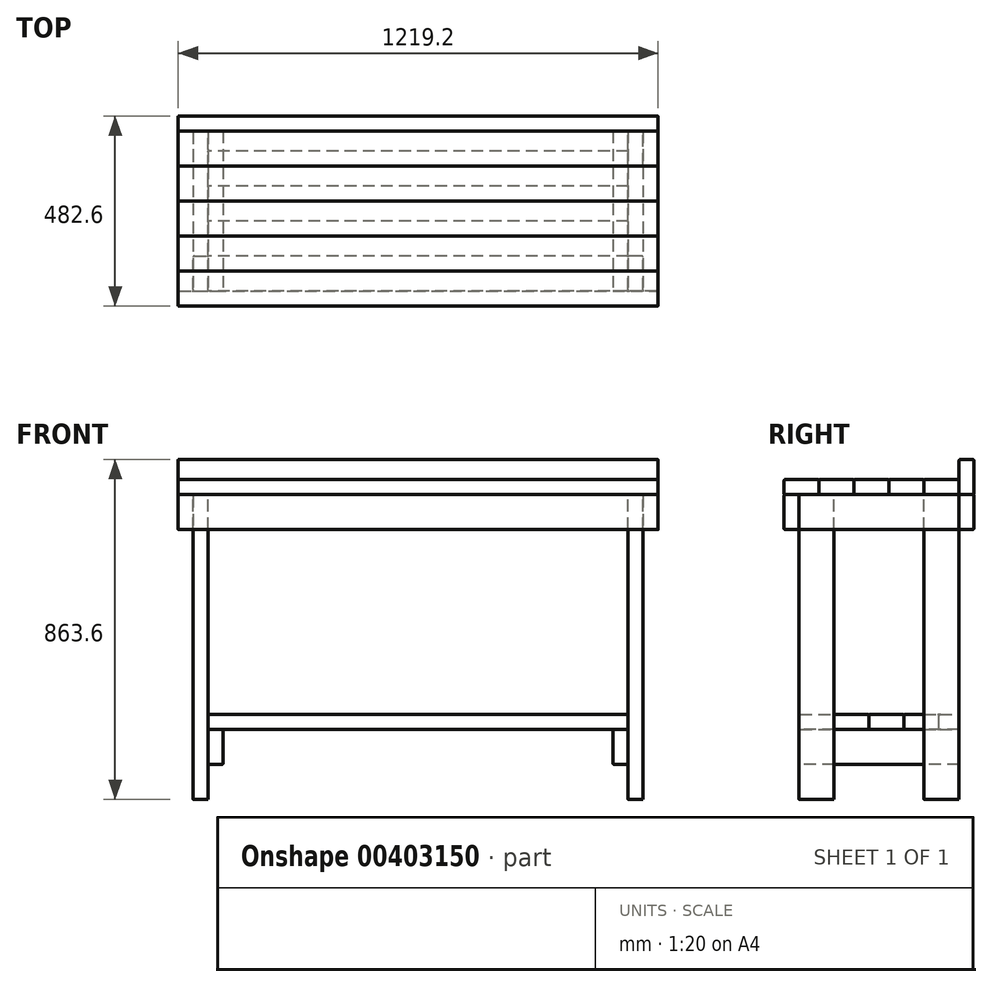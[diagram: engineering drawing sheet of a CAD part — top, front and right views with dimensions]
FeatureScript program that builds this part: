
annotation { "Feature Type Name" : "Feature", "Feature Type Description" : "" }
export const myFeature = defineFeature(function(context is Context, id is Id, definition is map)
    precondition{}
    {
        {
            var Q0;
            Q0=qCreatedBy(makeId("Right.planeOp"),FACE);
            var sketch = newSketch(context, id + "F0", { "sketchPlane" : qUnion([Q0])});
            skLineSegment(sketch, "E0.bottom", {"start": v(3.17, 0) * mm, "end": v(85.73, 0) * mm});
            skLineSegment(sketch, "E0.top", {"start": v(3.17, 38.1) * mm, "end": v(85.73, 38.1) * mm});
            skLineSegment(sketch, "E0.left", {"start": v(0, 3.18) * mm, "end": v(0, 34.93) * mm});
            skLineSegment(sketch, "E0.right", {"start": v(88.9, 3.18) * mm, "end": v(88.9, 34.93) * mm});
            skPoint(sketch, "E1.visualSharp", {"position": v(0, 38.1) * mm});
            skArc(sketch, "E1.filletArc", {"start": v(3.17, 38.1) * mm, "mid": v(0.93, 37.17) * mm, "end": v(0, 34.93) * mm});
            skPoint(sketch, "E2.visualSharp", {"position": v(0, 0) * mm});
            skArc(sketch, "E2.filletArc", {"start": v(0, 3.18) * mm, "mid": v(0.93, 0.93) * mm, "end": v(3.17, 0) * mm});
            skPoint(sketch, "E3.visualSharp", {"position": v(88.9, 0) * mm});
            skArc(sketch, "E3.filletArc", {"start": v(85.73, 0) * mm, "mid": v(87.97, 0.93) * mm, "end": v(88.9, 3.18) * mm});
            skPoint(sketch, "E4.visualSharp", {"position": v(88.9, 38.1) * mm});
            skArc(sketch, "E4.filletArc", {"start": v(88.9, 34.93) * mm, "mid": v(87.97, 37.17) * mm, "end": v(85.73, 38.1) * mm});
            skSolve(sketch);
        }
        {
            var Q0;
            Q0 = qSketchRegion(id + "F0", true);
            extrude(context, id + "F1", {"entities" : qUnion([Q0]), "depth" : 1219.2 * mm});
        }
        {
            var Q0;
            Q0=makeQuery(id+"F1.opExtrude","SWEPT_BODY",BODY,{"disambiguationData":[OSD([sQuery(id+"F0.wireOp",EDGE,"E0.bottom"),sQuery(id+"F0.wireOp",EDGE,"E0.top"),sQuery(id+"F0.wireOp",EDGE,"E0.left"),sQuery(id+"F0.wireOp",EDGE,"E0.right"),sQuery(id+"F0.wireOp",EDGE,"E1.filletArc"),sQuery(id+"F0.wireOp",EDGE,"E2.filletArc"),sQuery(id+"F0.wireOp",EDGE,"E3.filletArc"),sQuery(id+"F0.wireOp",EDGE,"E4.filletArc")])]});
            transform(context, id + "F2", {"entities" : qUnion([Q0]), "transformType" : TransformType.TRANSLATION_3D, "dx" : 0 * mm, "dy" : 88.9 * mm, "dz" : 0 * mm, "makeCopy" : true});
        }
        {
            var Q0;
            Q0=makeQuery(id+"F2.opPattern","COPY",BODY,{"derivedFrom":makeQuery(id+"F1.opExtrude","SWEPT_BODY",BODY,{"disambiguationData":[OSD([sQuery(id+"F0.wireOp",EDGE,"E0.bottom"),sQuery(id+"F0.wireOp",EDGE,"E0.top"),sQuery(id+"F0.wireOp",EDGE,"E0.left"),sQuery(id+"F0.wireOp",EDGE,"E0.right"),sQuery(id+"F0.wireOp",EDGE,"E1.filletArc"),sQuery(id+"F0.wireOp",EDGE,"E2.filletArc"),sQuery(id+"F0.wireOp",EDGE,"E3.filletArc"),sQuery(id+"F0.wireOp",EDGE,"E4.filletArc")])]}),"instanceName":"1"});
            transform(context, id + "F3", {"entities" : qUnion([Q0]), "transformType" : TransformType.TRANSLATION_3D, "dx" : 0 * mm, "dy" : 88.9 * mm, "dz" : 0 * mm, "makeCopy" : true});
        }
        {
            var Q0;
            Q0=makeQuery(id+"F3.opPattern","COPY",BODY,{"derivedFrom":makeQuery(id+"F2.opPattern","COPY",BODY,{"derivedFrom":makeQuery(id+"F1.opExtrude","SWEPT_BODY",BODY,{"disambiguationData":[OSD([sQuery(id+"F0.wireOp",EDGE,"E0.bottom"),sQuery(id+"F0.wireOp",EDGE,"E0.top"),sQuery(id+"F0.wireOp",EDGE,"E0.left"),sQuery(id+"F0.wireOp",EDGE,"E0.right"),sQuery(id+"F0.wireOp",EDGE,"E1.filletArc"),sQuery(id+"F0.wireOp",EDGE,"E2.filletArc"),sQuery(id+"F0.wireOp",EDGE,"E3.filletArc"),sQuery(id+"F0.wireOp",EDGE,"E4.filletArc")])]}),"instanceName":"1"}),"instanceName":"1"});
            transform(context, id + "F4", {"entities" : qUnion([Q0]), "transformType" : TransformType.TRANSLATION_3D, "dx" : 0 * mm, "dy" : 88.9 * mm, "dz" : 0 * mm, "makeCopy" : true});
        }
        {
            var Q0;
            Q0=makeQuery(id+"F4.opPattern","COPY",BODY,{"derivedFrom":makeQuery(id+"F3.opPattern","COPY",BODY,{"derivedFrom":makeQuery(id+"F2.opPattern","COPY",BODY,{"derivedFrom":makeQuery(id+"F1.opExtrude","SWEPT_BODY",BODY,{"disambiguationData":[OSD([sQuery(id+"F0.wireOp",EDGE,"E0.bottom"),sQuery(id+"F0.wireOp",EDGE,"E0.top"),sQuery(id+"F0.wireOp",EDGE,"E0.left"),sQuery(id+"F0.wireOp",EDGE,"E0.right"),sQuery(id+"F0.wireOp",EDGE,"E1.filletArc"),sQuery(id+"F0.wireOp",EDGE,"E2.filletArc"),sQuery(id+"F0.wireOp",EDGE,"E3.filletArc"),sQuery(id+"F0.wireOp",EDGE,"E4.filletArc")])]}),"instanceName":"1"}),"instanceName":"1"}),"instanceName":"1"});
            transform(context, id + "F5", {"entities" : qUnion([Q0]), "transformType" : TransformType.TRANSLATION_3D, "dx" : 0 * mm, "dy" : 88.9 * mm, "dz" : 0 * mm, "makeCopy" : true});
        }
        {
            var Q0;
            Q0=qCreatedBy(makeId("Right.planeOp"),FACE);
            var sketch = newSketch(context, id + "F6", { "sketchPlane" : qUnion([Q0])});
            skLineSegment(sketch, "E5.bottom", {"start": v(447.68, 0) * mm, "end": v(479.43, 0) * mm});
            skLineSegment(sketch, "E5.top", {"start": v(447.68, 88.9) * mm, "end": v(479.43, 88.9) * mm});
            skLineSegment(sketch, "E5.left", {"start": v(444.5, 3.18) * mm, "end": v(444.5, 85.73) * mm});
            skLineSegment(sketch, "E5.right", {"start": v(482.6, 3.17) * mm, "end": v(482.6, 85.73) * mm});
            skPoint(sketch, "E6.visualSharp", {"position": v(444.5, 88.9) * mm});
            skArc(sketch, "E6.filletArc", {"start": v(447.68, 88.9) * mm, "mid": v(445.43, 87.97) * mm, "end": v(444.5, 85.73) * mm});
            skPoint(sketch, "E7.visualSharp", {"position": v(482.6, 88.9) * mm});
            skArc(sketch, "E7.filletArc", {"start": v(482.6, 85.73) * mm, "mid": v(481.67, 87.97) * mm, "end": v(479.43, 88.9) * mm});
            skPoint(sketch, "E8.visualSharp", {"position": v(482.6, 0) * mm});
            skArc(sketch, "E8.filletArc", {"start": v(479.43, 0) * mm, "mid": v(481.67, 0.93) * mm, "end": v(482.6, 3.17) * mm});
            skPoint(sketch, "E9.visualSharp", {"position": v(444.5, 0) * mm});
            skArc(sketch, "E9.filletArc", {"start": v(444.5, 3.18) * mm, "mid": v(445.43, 0.93) * mm, "end": v(447.68, 0) * mm});
            skSolve(sketch);
        }
        {
            var Q0;
            Q0 = qSketchRegion(id + "F6", true);
            extrude(context, id + "F7", {"entities" : qUnion([Q0]), "depth" : 1219.2 * mm});
        }
        {
            var Q0;
            Q0=makeQuery(id+"F1.opExtrude","CAP_FACE",FACE,{"disambiguationData":[OSD([sQuery(id+"F0.wireOp",EDGE,"E0.bottom"),sQuery(id+"F0.wireOp",EDGE,"E0.top"),sQuery(id+"F0.wireOp",EDGE,"E0.left"),sQuery(id+"F0.wireOp",EDGE,"E0.right"),sQuery(id+"F0.wireOp",EDGE,"E1.filletArc"),sQuery(id+"F0.wireOp",EDGE,"E2.filletArc"),sQuery(id+"F0.wireOp",EDGE,"E3.filletArc"),sQuery(id+"F0.wireOp",EDGE,"E4.filletArc")])],"isStart":false});
            var sketch = newSketch(context, id + "F8", { "sketchPlane" : qUnion([Q0])});
            skLineSegment(sketch, "E10.bottom", {"start": v(3.18, 0) * mm, "end": v(34.93, 0) * mm});
            skLineSegment(sketch, "E10.top", {"start": v(3.18, -88.9) * mm, "end": v(34.93, -88.9) * mm});
            skLineSegment(sketch, "E10.left", {"start": v(0, -3.17) * mm, "end": v(0, -85.72) * mm});
            skLineSegment(sketch, "E10.right", {"start": v(38.1, -3.17) * mm, "end": v(38.1, -85.72) * mm});
            skPoint(sketch, "E11.visualSharp", {"position": v(0, 0) * mm});
            skArc(sketch, "E11.filletArc", {"start": v(3.18, 0) * mm, "mid": v(0.93, -0.93) * mm, "end": v(0, -3.18) * mm});
            skPoint(sketch, "E12.visualSharp", {"position": v(38.1, 0) * mm});
            skArc(sketch, "E12.filletArc", {"start": v(38.1, -3.17) * mm, "mid": v(37.17, -0.93) * mm, "end": v(34.93, 0) * mm});
            skPoint(sketch, "E13.visualSharp", {"position": v(38.1, -88.9) * mm});
            skArc(sketch, "E13.filletArc", {"start": v(34.93, -88.9) * mm, "mid": v(37.17, -87.97) * mm, "end": v(38.1, -85.72) * mm});
            skPoint(sketch, "E14.visualSharp", {"position": v(0, -88.9) * mm});
            skArc(sketch, "E14.filletArc", {"start": v(0, -85.72) * mm, "mid": v(0.93, -87.97) * mm, "end": v(3.18, -88.9) * mm});
            skSolve(sketch);
        }
        {
            var Q0;
            Q0 = qSketchRegion(id + "F8", true);
            extrude(context, id + "F9", {"entities" : qUnion([Q0]), "oppositeDirection" : true, "depth" : 1219.2 * mm});
        }
        {
            var Q0;
            Q0=makeQuery(id+"F7.opExtrude","CAP_FACE",FACE,{"disambiguationData":[OSD([sQuery(id+"F6.wireOp",EDGE,"E5.bottom"),sQuery(id+"F6.wireOp",EDGE,"E5.top"),sQuery(id+"F6.wireOp",EDGE,"E5.left"),sQuery(id+"F6.wireOp",EDGE,"E5.right"),sQuery(id+"F6.wireOp",EDGE,"E6.filletArc"),sQuery(id+"F6.wireOp",EDGE,"E7.filletArc"),sQuery(id+"F6.wireOp",EDGE,"E8.filletArc"),sQuery(id+"F6.wireOp",EDGE,"E9.filletArc")])],"isStart":false});
            var sketch = newSketch(context, id + "F10", { "sketchPlane" : qUnion([Q0])});
            skLineSegment(sketch, "E15.bottom", {"start": v(447.68, 0) * mm, "end": v(479.43, 0) * mm});
            skLineSegment(sketch, "E15.top", {"start": v(447.68, -88.9) * mm, "end": v(479.43, -88.9) * mm});
            skLineSegment(sketch, "E15.left", {"start": v(444.5, -3.17) * mm, "end": v(444.5, -85.73) * mm});
            skLineSegment(sketch, "E15.right", {"start": v(482.6, -3.17) * mm, "end": v(482.6, -85.73) * mm});
            skPoint(sketch, "E16.visualSharp", {"position": v(444.5, 0) * mm});
            skArc(sketch, "E16.filletArc", {"start": v(447.68, 0) * mm, "mid": v(445.43, -0.93) * mm, "end": v(444.5, -3.17) * mm});
            skPoint(sketch, "E17.visualSharp", {"position": v(482.6, 0) * mm});
            skArc(sketch, "E17.filletArc", {"start": v(482.6, -3.17) * mm, "mid": v(481.67, -0.93) * mm, "end": v(479.43, 0) * mm});
            skPoint(sketch, "E18.visualSharp", {"position": v(482.6, -88.9) * mm});
            skArc(sketch, "E18.filletArc", {"start": v(479.43, -88.9) * mm, "mid": v(481.67, -87.97) * mm, "end": v(482.6, -85.73) * mm});
            skPoint(sketch, "E19.visualSharp", {"position": v(444.5, -88.9) * mm});
            skArc(sketch, "E19.filletArc", {"start": v(444.5, -85.73) * mm, "mid": v(445.43, -87.97) * mm, "end": v(447.68, -88.9) * mm});
            skSolve(sketch);
        }
        {
            var Q0;
            Q0 = qSketchRegion(id + "F10", true);
            extrude(context, id + "F11", {"entities" : qUnion([Q0]), "oppositeDirection" : true, "depth" : 1219.2 * mm});
        }
        {
            var Q0;
            Q0=makeQuery(id+"F9.opExtrude","SWEPT_FACE",FACE,{"disambiguationData":[OSD([sQuery(id+"F8.wireOp",EDGE,"E10.right")])]});
            var sketch = newSketch(context, id + "F12", { "sketchPlane" : qUnion([Q0])});
            skLineSegment(sketch, "E20.bottom", {"start": v(-1215.47, 0) * mm, "end": v(-1183.72, 0) * mm});
            skLineSegment(sketch, "E20.top", {"start": v(-1215.47, -88.9) * mm, "end": v(-1183.72, -88.9) * mm});
            skLineSegment(sketch, "E20.left", {"start": v(-1218.64, -3.17) * mm, "end": v(-1218.64, -85.73) * mm});
            skLineSegment(sketch, "E20.right", {"start": v(-1180.54, -3.17) * mm, "end": v(-1180.54, -85.73) * mm});
            skPoint(sketch, "E21.visualSharp", {"position": v(-1218.64, 0) * mm});
            skArc(sketch, "E21.filletArc", {"start": v(-1215.47, 0) * mm, "mid": v(-1217.71, -0.93) * mm, "end": v(-1218.64, -3.17) * mm});
            skPoint(sketch, "E22.visualSharp", {"position": v(-1180.54, 0) * mm});
            skArc(sketch, "E22.filletArc", {"start": v(-1180.54, -3.17) * mm, "mid": v(-1181.47, -0.93) * mm, "end": v(-1183.72, 0) * mm});
            skPoint(sketch, "E23.visualSharp", {"position": v(-1180.54, -88.9) * mm});
            skArc(sketch, "E23.filletArc", {"start": v(-1183.72, -88.9) * mm, "mid": v(-1181.47, -87.97) * mm, "end": v(-1180.54, -85.73) * mm});
            skPoint(sketch, "E24.visualSharp", {"position": v(-1218.64, -88.9) * mm});
            skArc(sketch, "E24.filletArc", {"start": v(-1218.64, -85.73) * mm, "mid": v(-1217.71, -87.97) * mm, "end": v(-1215.47, -88.9) * mm});
            skSolve(sketch);
        }
        {
            var Q0;
            Q0 = qSketchRegion(id + "F12", true);
            extrude(context, id + "F13", {"entities" : qUnion([Q0]), "depth" : 406.4 * mm});
        }
        {
            var Q0;
            Q0=makeQuery(id+"F9.opExtrude","SWEPT_FACE",FACE,{"disambiguationData":[OSD([sQuery(id+"F8.wireOp",EDGE,"E10.right")])]});
            var sketch = newSketch(context, id + "F14", { "sketchPlane" : qUnion([Q0])});
            skLineSegment(sketch, "E25.bottom", {"start": v(-3.18, 0) * mm, "end": v(-34.92, 0) * mm});
            skLineSegment(sketch, "E25.top", {"start": v(-3.18, -88.9) * mm, "end": v(-34.92, -88.9) * mm});
            skLineSegment(sketch, "E25.left", {"start": v(0, -3.17) * mm, "end": v(0, -85.73) * mm});
            skLineSegment(sketch, "E25.right", {"start": v(-38.1, -3.17) * mm, "end": v(-38.1, -85.73) * mm});
            skPoint(sketch, "E26.visualSharp", {"position": v(-38.1, 0) * mm});
            skArc(sketch, "E26.filletArc", {"start": v(-34.92, 0) * mm, "mid": v(-37.17, -0.93) * mm, "end": v(-38.1, -3.17) * mm});
            skPoint(sketch, "E27.visualSharp", {"position": v(0, 0) * mm});
            skArc(sketch, "E27.filletArc", {"start": v(0, -3.17) * mm, "mid": v(-0.93, -0.93) * mm, "end": v(-3.18, 0) * mm});
            skPoint(sketch, "E28.visualSharp", {"position": v(0, -88.9) * mm});
            skArc(sketch, "E28.filletArc", {"start": v(-3.18, -88.9) * mm, "mid": v(-0.93, -87.97) * mm, "end": v(0, -85.73) * mm});
            skPoint(sketch, "E29.visualSharp", {"position": v(-38.1, -88.9) * mm});
            skArc(sketch, "E29.filletArc", {"start": v(-38.1, -85.73) * mm, "mid": v(-37.17, -87.97) * mm, "end": v(-34.92, -88.9) * mm});
            skSolve(sketch);
        }
        {
            var Q0;
            Q0 = qSketchRegion(id + "F14", true);
            extrude(context, id + "F15", {"entities" : qUnion([Q0]), "depth" : 406.4 * mm});
        }
        {
            var Q0;
            Q0=makeQuery(id+"F5.opPattern","COPY",FACE,{"derivedFrom":makeQuery(id+"F4.opPattern","COPY",FACE,{"derivedFrom":makeQuery(id+"F3.opPattern","COPY",FACE,{"derivedFrom":makeQuery(id+"F2.opPattern","COPY",FACE,{"derivedFrom":makeQuery(id+"F1.opExtrude","SWEPT_FACE",FACE,{"disambiguationData":[OSD([sQuery(id+"F0.wireOp",EDGE,"E0.bottom")])]}),"instanceName":"1"}),"instanceName":"1"}),"instanceName":"1"}),"instanceName":"1"});
            var sketch = newSketch(context, id + "F16", { "sketchPlane" : qUnion([Q0])});
            skLineSegment(sketch, "E30.bottom", {"start": v(1177.93, -355.7) * mm, "end": v(1146.17, -355.7) * mm});
            skLineSegment(sketch, "E30.top", {"start": v(1177.93, -444.5) * mm, "end": v(1146.17, -444.5) * mm});
            skLineSegment(sketch, "E30.left", {"start": v(1181.1, -358.87) * mm, "end": v(1181.1, -441.32) * mm});
            skLineSegment(sketch, "E30.right", {"start": v(1143, -358.87) * mm, "end": v(1143, -441.32) * mm});
            skPoint(sketch, "E31.visualSharp", {"position": v(1143, -355.7) * mm});
            skArc(sketch, "E31.filletArc", {"start": v(1146.17, -355.7) * mm, "mid": v(1143.93, -356.63) * mm, "end": v(1143, -358.87) * mm});
            skPoint(sketch, "E32.visualSharp", {"position": v(1143, -444.5) * mm});
            skArc(sketch, "E32.filletArc", {"start": v(1143, -441.32) * mm, "mid": v(1143.93, -443.57) * mm, "end": v(1146.17, -444.5) * mm});
            skPoint(sketch, "E33.visualSharp", {"position": v(1181.1, -444.5) * mm});
            skArc(sketch, "E33.filletArc", {"start": v(1177.93, -444.5) * mm, "mid": v(1180.17, -443.57) * mm, "end": v(1181.1, -441.32) * mm});
            skPoint(sketch, "E34.visualSharp", {"position": v(1181.1, -355.7) * mm});
            skArc(sketch, "E34.filletArc", {"start": v(1181.1, -358.87) * mm, "mid": v(1180.17, -356.63) * mm, "end": v(1177.93, -355.7) * mm});
            skSolve(sketch);
        }
        {
            var Q0;
            Q0 = qSketchRegion(id + "F16", true);
            extrude(context, id + "F17", {"entities" : qUnion([Q0]), "depth" : 774.7 * mm});
        }
        {
            var Q0;
            Q0=makeQuery(id+"F1.opExtrude","SWEPT_FACE",FACE,{"disambiguationData":[OSD([sQuery(id+"F0.wireOp",EDGE,"E0.bottom")])]});
            var sketch = newSketch(context, id + "F18", { "sketchPlane" : qUnion([Q0])});
            skLineSegment(sketch, "E35.bottom", {"start": v(1177.93, -38.1) * mm, "end": v(1146.17, -38.1) * mm});
            skLineSegment(sketch, "E35.top", {"start": v(1177.93, -127) * mm, "end": v(1146.17, -127) * mm});
            skLineSegment(sketch, "E35.left", {"start": v(1181.1, -41.27) * mm, "end": v(1181.1, -123.83) * mm});
            skLineSegment(sketch, "E35.right", {"start": v(1143, -41.27) * mm, "end": v(1143, -123.83) * mm});
            skPoint(sketch, "E36.visualSharp", {"position": v(1181.1, -38.1) * mm});
            skArc(sketch, "E36.filletArc", {"start": v(1181.1, -41.27) * mm, "mid": v(1180.17, -39.03) * mm, "end": v(1177.93, -38.1) * mm});
            skPoint(sketch, "E37.visualSharp", {"position": v(1143, -38.1) * mm});
            skArc(sketch, "E37.filletArc", {"start": v(1146.17, -38.1) * mm, "mid": v(1143.93, -39.03) * mm, "end": v(1143, -41.27) * mm});
            skPoint(sketch, "E38.visualSharp", {"position": v(1143, -127) * mm});
            skArc(sketch, "E38.filletArc", {"start": v(1143, -123.83) * mm, "mid": v(1143.93, -126.07) * mm, "end": v(1146.17, -127) * mm});
            skPoint(sketch, "E39.visualSharp", {"position": v(1181.1, -127) * mm});
            skArc(sketch, "E39.filletArc", {"start": v(1177.93, -127) * mm, "mid": v(1180.17, -126.07) * mm, "end": v(1181.1, -123.83) * mm});
            skSolve(sketch);
        }
        {
            var Q0;
            Q0=makeQuery(id+"F18.imprint","IMPRINT",FACE,{"disambiguationData":[TD([[makeQuery(id+"F18.imprint","IMPRINT",EDGE,{"derivedFrom":sQuery(id+"F18.wireOp",EDGE,"E35.bottom")}),1.0]])]});
            var Q1;
            Q1 = qSketchRegion(id + "F18", true);
            extrude(context, id + "F19", {"entities" : qUnion([Q0, Q1]), "depth" : 774.7 * mm});
        }
        {
            var Q0;
            Q0=makeQuery(id+"F5.opPattern","COPY",FACE,{"derivedFrom":makeQuery(id+"F4.opPattern","COPY",FACE,{"derivedFrom":makeQuery(id+"F3.opPattern","COPY",FACE,{"derivedFrom":makeQuery(id+"F2.opPattern","COPY",FACE,{"derivedFrom":makeQuery(id+"F1.opExtrude","SWEPT_FACE",FACE,{"disambiguationData":[OSD([sQuery(id+"F0.wireOp",EDGE,"E0.bottom")])]}),"instanceName":"1"}),"instanceName":"1"}),"instanceName":"1"}),"instanceName":"1"});
            var sketch = newSketch(context, id + "F20", { "sketchPlane" : qUnion([Q0])});
            skLineSegment(sketch, "E40.bottom", {"start": v(41.28, -444.5) * mm, "end": v(73.03, -444.5) * mm});
            skLineSegment(sketch, "E40.top", {"start": v(41.27, -355.6) * mm, "end": v(73.03, -355.6) * mm});
            skLineSegment(sketch, "E40.left", {"start": v(38.1, -441.32) * mm, "end": v(38.1, -358.77) * mm});
            skLineSegment(sketch, "E40.right", {"start": v(76.2, -441.32) * mm, "end": v(76.2, -358.77) * mm});
            skPoint(sketch, "E41.visualSharp", {"position": v(76.2, -355.6) * mm});
            skArc(sketch, "E41.filletArc", {"start": v(76.2, -358.77) * mm, "mid": v(75.27, -356.53) * mm, "end": v(73.03, -355.6) * mm});
            skPoint(sketch, "E42.visualSharp", {"position": v(38.1, -355.6) * mm});
            skArc(sketch, "E42.filletArc", {"start": v(41.27, -355.6) * mm, "mid": v(39.03, -356.53) * mm, "end": v(38.1, -358.77) * mm});
            skPoint(sketch, "E43.visualSharp", {"position": v(38.1, -444.5) * mm});
            skArc(sketch, "E43.filletArc", {"start": v(38.1, -441.32) * mm, "mid": v(39.03, -443.57) * mm, "end": v(41.28, -444.5) * mm});
            skPoint(sketch, "E44.visualSharp", {"position": v(76.2, -444.5) * mm});
            skArc(sketch, "E44.filletArc", {"start": v(73.03, -444.5) * mm, "mid": v(75.27, -443.57) * mm, "end": v(76.2, -441.32) * mm});
            skSolve(sketch);
        }
        {
            var Q0;
            Q0 = qSketchRegion(id + "F20", true);
            extrude(context, id + "F21", {"entities" : qUnion([Q0]), "depth" : 774.7 * mm});
        }
        {
            var Q0;
            Q0=makeQuery(id+"F1.opExtrude","SWEPT_FACE",FACE,{"disambiguationData":[OSD([sQuery(id+"F0.wireOp",EDGE,"E0.bottom")])]});
            var sketch = newSketch(context, id + "F22", { "sketchPlane" : qUnion([Q0])});
            skLineSegment(sketch, "E45.bottom", {"start": v(41.27, -38.1) * mm, "end": v(73.03, -38.1) * mm});
            skLineSegment(sketch, "E45.top", {"start": v(41.28, -127) * mm, "end": v(73.03, -127) * mm});
            skLineSegment(sketch, "E45.left", {"start": v(38.1, -41.27) * mm, "end": v(38.1, -123.83) * mm});
            skLineSegment(sketch, "E45.right", {"start": v(76.2, -41.27) * mm, "end": v(76.2, -123.83) * mm});
            skPoint(sketch, "E46.visualSharp", {"position": v(76.2, -38.1) * mm});
            skArc(sketch, "E46.filletArc", {"start": v(76.2, -41.27) * mm, "mid": v(75.27, -39.03) * mm, "end": v(73.03, -38.1) * mm});
            skPoint(sketch, "E47.visualSharp", {"position": v(38.1, -38.1) * mm});
            skArc(sketch, "E47.filletArc", {"start": v(41.27, -38.1) * mm, "mid": v(39.03, -39.03) * mm, "end": v(38.1, -41.27) * mm});
            skPoint(sketch, "E48.visualSharp", {"position": v(38.1, -127) * mm});
            skArc(sketch, "E48.filletArc", {"start": v(38.1, -123.83) * mm, "mid": v(39.03, -126.07) * mm, "end": v(41.28, -127) * mm});
            skPoint(sketch, "E49.visualSharp", {"position": v(76.2, -127) * mm});
            skArc(sketch, "E49.filletArc", {"start": v(73.03, -127) * mm, "mid": v(75.27, -126.07) * mm, "end": v(76.2, -123.83) * mm});
            skSolve(sketch);
        }
        {
            var Q0;
            Q0 = qSketchRegion(id + "F22", true);
            extrude(context, id + "F23", {"entities" : qUnion([Q0]), "depth" : 774.7 * mm});
        }
        {
            var Q0;
            Q0=makeQuery(id+"F9.opExtrude","SWEPT_BODY",BODY,{"disambiguationData":[OSD([sQuery(id+"F8.wireOp",EDGE,"E10.bottom"),sQuery(id+"F8.wireOp",EDGE,"E10.top"),sQuery(id+"F8.wireOp",EDGE,"E10.left"),sQuery(id+"F8.wireOp",EDGE,"E10.right"),sQuery(id+"F8.wireOp",EDGE,"E11.filletArc"),sQuery(id+"F8.wireOp",EDGE,"E12.filletArc"),sQuery(id+"F8.wireOp",EDGE,"E13.filletArc"),sQuery(id+"F8.wireOp",EDGE,"E14.filletArc")])]});
            transform(context, id + "F24", {"entities" : qUnion([Q0]), "transformType" : TransformType.TRANSLATION_3D, "dx" : 0 * mm, "dy" : 0 * mm, "dz" : -558.8 * mm, "makeCopy" : true});
        }
        {
            var Q0;
            Q0=makeQuery(id+"F13.opExtrude","SWEPT_BODY",BODY,{"disambiguationData":[OSD([sQuery(id+"F12.wireOp",EDGE,"E20.bottom"),sQuery(id+"F12.wireOp",EDGE,"E20.top"),sQuery(id+"F12.wireOp",EDGE,"E20.left"),sQuery(id+"F12.wireOp",EDGE,"E20.right"),sQuery(id+"F12.wireOp",EDGE,"E21.filletArc"),sQuery(id+"F12.wireOp",EDGE,"E22.filletArc"),sQuery(id+"F12.wireOp",EDGE,"E23.filletArc"),sQuery(id+"F12.wireOp",EDGE,"E24.filletArc")])]});
            transform(context, id + "F25", {"entities" : qUnion([Q0]), "transformType" : TransformType.TRANSLATION_3D, "dx" : 0 * mm, "dy" : 0 * mm, "dz" : -558.8 * mm, "makeCopy" : true});
        }
        {
            var Q0;
            Q0=makeQuery(id+"F11.opExtrude","SWEPT_BODY",BODY,{"disambiguationData":[OSD([sQuery(id+"F10.wireOp",EDGE,"E15.bottom"),sQuery(id+"F10.wireOp",EDGE,"E15.top"),sQuery(id+"F10.wireOp",EDGE,"E15.left"),sQuery(id+"F10.wireOp",EDGE,"E15.right"),sQuery(id+"F10.wireOp",EDGE,"E16.filletArc"),sQuery(id+"F10.wireOp",EDGE,"E17.filletArc"),sQuery(id+"F10.wireOp",EDGE,"E18.filletArc"),sQuery(id+"F10.wireOp",EDGE,"E19.filletArc")])]});
            transform(context, id + "F26", {"entities" : qUnion([Q0]), "transformType" : TransformType.TRANSLATION_3D, "dx" : 0 * mm, "dy" : 0 * mm, "dz" : -558.8 * mm, "makeCopy" : true});
        }
        {
            var Q0;
            Q0=makeQuery(id+"F15.opExtrude","SWEPT_BODY",BODY,{"disambiguationData":[OSD([sQuery(id+"F14.wireOp",EDGE,"E25.bottom"),sQuery(id+"F14.wireOp",EDGE,"E25.top"),sQuery(id+"F14.wireOp",EDGE,"E25.left"),sQuery(id+"F14.wireOp",EDGE,"E25.right"),sQuery(id+"F14.wireOp",EDGE,"E26.filletArc"),sQuery(id+"F14.wireOp",EDGE,"E27.filletArc"),sQuery(id+"F14.wireOp",EDGE,"E28.filletArc"),sQuery(id+"F14.wireOp",EDGE,"E29.filletArc")])]});
            transform(context, id + "F27", {"entities" : qUnion([Q0]), "transformType" : TransformType.TRANSLATION_3D, "dx" : 0 * mm, "dy" : 0 * mm, "dz" : -558.8 * mm, "makeCopy" : true});
        }
        {
            var Q0;
            Q0=makeQuery(id+"F27.opPattern","COPY",BODY,{"derivedFrom":makeQuery(id+"F15.opExtrude","SWEPT_BODY",BODY,{"disambiguationData":[OSD([sQuery(id+"F14.wireOp",EDGE,"E25.bottom"),sQuery(id+"F14.wireOp",EDGE,"E25.top"),sQuery(id+"F14.wireOp",EDGE,"E25.left"),sQuery(id+"F14.wireOp",EDGE,"E25.right"),sQuery(id+"F14.wireOp",EDGE,"E26.filletArc"),sQuery(id+"F14.wireOp",EDGE,"E27.filletArc"),sQuery(id+"F14.wireOp",EDGE,"E28.filletArc"),sQuery(id+"F14.wireOp",EDGE,"E29.filletArc")])]}),"instanceName":"1"});
            deleteBodies(context, id + "F28", {"entities" : qUnion([Q0])});
        }
        {
            var Q0;
            Q0=makeQuery(id+"F25.opPattern","COPY",BODY,{"derivedFrom":makeQuery(id+"F13.opExtrude","SWEPT_BODY",BODY,{"disambiguationData":[OSD([sQuery(id+"F12.wireOp",EDGE,"E20.bottom"),sQuery(id+"F12.wireOp",EDGE,"E20.top"),sQuery(id+"F12.wireOp",EDGE,"E20.left"),sQuery(id+"F12.wireOp",EDGE,"E20.right"),sQuery(id+"F12.wireOp",EDGE,"E21.filletArc"),sQuery(id+"F12.wireOp",EDGE,"E22.filletArc"),sQuery(id+"F12.wireOp",EDGE,"E23.filletArc"),sQuery(id+"F12.wireOp",EDGE,"E24.filletArc")])]}),"instanceName":"1"});
            deleteBodies(context, id + "F29", {"entities" : qUnion([Q0])});
        }
        {
            var Q0;
            Q0=makeQuery(id+"F26.opPattern","COPY",BODY,{"derivedFrom":makeQuery(id+"F11.opExtrude","SWEPT_BODY",BODY,{"disambiguationData":[OSD([sQuery(id+"F10.wireOp",EDGE,"E15.bottom"),sQuery(id+"F10.wireOp",EDGE,"E15.top"),sQuery(id+"F10.wireOp",EDGE,"E15.left"),sQuery(id+"F10.wireOp",EDGE,"E15.right"),sQuery(id+"F10.wireOp",EDGE,"E16.filletArc"),sQuery(id+"F10.wireOp",EDGE,"E17.filletArc"),sQuery(id+"F10.wireOp",EDGE,"E18.filletArc"),sQuery(id+"F10.wireOp",EDGE,"E19.filletArc")])]}),"instanceName":"1"});
            deleteBodies(context, id + "F30", {"entities" : qUnion([Q0])});
        }
        {
            var Q0;
            Q0=makeQuery(id+"F24.opPattern","COPY",BODY,{"derivedFrom":makeQuery(id+"F9.opExtrude","SWEPT_BODY",BODY,{"disambiguationData":[OSD([sQuery(id+"F8.wireOp",EDGE,"E10.bottom"),sQuery(id+"F8.wireOp",EDGE,"E10.top"),sQuery(id+"F8.wireOp",EDGE,"E10.left"),sQuery(id+"F8.wireOp",EDGE,"E10.right"),sQuery(id+"F8.wireOp",EDGE,"E11.filletArc"),sQuery(id+"F8.wireOp",EDGE,"E12.filletArc"),sQuery(id+"F8.wireOp",EDGE,"E13.filletArc"),sQuery(id+"F8.wireOp",EDGE,"E14.filletArc")])]}),"instanceName":"1"});
            deleteBodies(context, id + "F31", {"entities" : qUnion([Q0])});
        }
        {
            var Q0;
            Q0=makeQuery(id+"F23.opExtrude","SWEPT_FACE",FACE,{"disambiguationData":[OSD([sQuery(id+"F22.wireOp",EDGE,"E45.bottom")])]});
            var sketch = newSketch(context, id + "F32", { "sketchPlane" : qUnion([Q0])});
            skLineSegment(sketch, "E50.bottom", {"start": v(79.38, -685.8) * mm, "end": v(111.13, -685.8) * mm});
            skLineSegment(sketch, "E50.top", {"start": v(79.37, -596.9) * mm, "end": v(111.13, -596.9) * mm});
            skLineSegment(sketch, "E50.left", {"start": v(76.2, -682.62) * mm, "end": v(76.2, -600.08) * mm});
            skLineSegment(sketch, "E50.right", {"start": v(114.3, -682.62) * mm, "end": v(114.3, -600.08) * mm});
            skPoint(sketch, "E51.visualSharp", {"position": v(76.2, -596.9) * mm});
            skArc(sketch, "E51.filletArc", {"start": v(79.37, -596.9) * mm, "mid": v(77.13, -597.83) * mm, "end": v(76.2, -600.08) * mm});
            skPoint(sketch, "E52.visualSharp", {"position": v(114.3, -596.9) * mm});
            skArc(sketch, "E52.filletArc", {"start": v(114.3, -600.08) * mm, "mid": v(113.37, -597.83) * mm, "end": v(111.13, -596.9) * mm});
            skPoint(sketch, "E53.visualSharp", {"position": v(114.3, -685.8) * mm});
            skArc(sketch, "E53.filletArc", {"start": v(111.13, -685.8) * mm, "mid": v(113.37, -684.87) * mm, "end": v(114.3, -682.62) * mm});
            skPoint(sketch, "E54.visualSharp", {"position": v(76.2, -685.8) * mm});
            skArc(sketch, "E54.filletArc", {"start": v(76.2, -682.62) * mm, "mid": v(77.13, -684.87) * mm, "end": v(79.38, -685.8) * mm});
            skSolve(sketch);
        }
        {
            var Q0;
            Q0 = qSketchRegion(id + "F32", true);
            extrude(context, id + "F33", {"entities" : qUnion([Q0]), "oppositeDirection" : true, "depth" : 406.4 * mm});
        }
        {
            var Q0;
            Q0=makeQuery(id+"F23.opExtrude","SWEPT_FACE",FACE,{"disambiguationData":[OSD([sQuery(id+"F22.wireOp",EDGE,"E45.left")])]});
            var sketch = newSketch(context, id + "F34", { "sketchPlane" : qUnion([Q0])});
            skLineSegment(sketch, "E55.bottom", {"start": v(-34.93, -685.8) * mm, "end": v(-3.18, -685.8) * mm});
            skLineSegment(sketch, "E55.top", {"start": v(-34.92, -596.9) * mm, "end": v(-3.18, -596.9) * mm});
            skLineSegment(sketch, "E55.left", {"start": v(-38.1, -682.62) * mm, "end": v(-38.1, -600.08) * mm});
            skLineSegment(sketch, "E55.right", {"start": v(0, -682.62) * mm, "end": v(0, -600.08) * mm});
            skPoint(sketch, "E56.visualSharp", {"position": v(-38.1, -685.8) * mm});
            skArc(sketch, "E56.filletArc", {"start": v(-38.1, -682.62) * mm, "mid": v(-37.17, -684.87) * mm, "end": v(-34.93, -685.8) * mm});
            skPoint(sketch, "E57.visualSharp", {"position": v(0, -685.8) * mm});
            skArc(sketch, "E57.filletArc", {"start": v(-3.18, -685.8) * mm, "mid": v(-0.93, -684.87) * mm, "end": v(0, -682.62) * mm});
            skPoint(sketch, "E58.visualSharp", {"position": v(0, -596.9) * mm});
            skArc(sketch, "E58.filletArc", {"start": v(0, -600.08) * mm, "mid": v(-0.93, -597.83) * mm, "end": v(-3.18, -596.9) * mm});
            skPoint(sketch, "E59.visualSharp", {"position": v(-38.1, -596.9) * mm});
            skArc(sketch, "E59.filletArc", {"start": v(-34.93, -596.9) * mm, "mid": v(-37.17, -597.83) * mm, "end": v(-38.1, -600.08) * mm});
            skArc(sketch, "E60.filletArc", {"start": v(-34.92, -596.9) * mm, "mid": v(-37.17, -597.83) * mm, "end": v(-38.1, -600.08) * mm});
            skSolve(sketch);
        }
        {
            var Q0;
            Q0 = qSketchRegion(id + "F34", true);
            extrude(context, id + "F35", {"entities" : qUnion([Q0]), "oppositeDirection" : true, "depth" : 1143 * mm});
        }
        {
            var Q0;
            Q0=makeQuery(id+"F35.opExtrude","SWEPT_FACE",FACE,{"disambiguationData":[OSD([sQuery(id+"F34.wireOp",EDGE,"E55.left")])]});
            var sketch = newSketch(context, id + "F36", { "sketchPlane" : qUnion([Q0])});
            skLineSegment(sketch, "E61.bottom", {"start": v(-1139.82, -685.8) * mm, "end": v(-1108.08, -685.8) * mm});
            skLineSegment(sketch, "E61.top", {"start": v(-1139.82, -596.9) * mm, "end": v(-1108.08, -596.9) * mm});
            skLineSegment(sketch, "E61.left", {"start": v(-1143, -682.62) * mm, "end": v(-1143, -600.08) * mm});
            skLineSegment(sketch, "E61.right", {"start": v(-1104.9, -682.62) * mm, "end": v(-1104.9, -600.08) * mm});
            skPoint(sketch, "E62.visualSharp", {"position": v(-1143, -596.9) * mm});
            skArc(sketch, "E62.filletArc", {"start": v(-1139.82, -596.9) * mm, "mid": v(-1142.07, -597.83) * mm, "end": v(-1143, -600.08) * mm});
            skPoint(sketch, "E63.visualSharp", {"position": v(-1104.9, -596.9) * mm});
            skArc(sketch, "E63.filletArc", {"start": v(-1104.9, -600.08) * mm, "mid": v(-1105.83, -597.83) * mm, "end": v(-1108.08, -596.9) * mm});
            skPoint(sketch, "E64.visualSharp", {"position": v(-1104.9, -685.8) * mm});
            skArc(sketch, "E64.filletArc", {"start": v(-1108.08, -685.8) * mm, "mid": v(-1105.83, -684.87) * mm, "end": v(-1104.9, -682.62) * mm});
            skPoint(sketch, "E65.visualSharp", {"position": v(-1143, -685.8) * mm});
            skArc(sketch, "E65.filletArc", {"start": v(-1143, -682.62) * mm, "mid": v(-1142.07, -684.87) * mm, "end": v(-1139.82, -685.8) * mm});
            skSolve(sketch);
        }
        {
            var Q0;
            Q0 = qSketchRegion(id + "F36", true);
            extrude(context, id + "F37", {"entities" : qUnion([Q0]), "depth" : 406.4 * mm});
        }
        {
            var Q0;
            Q0=makeQuery(id+"F21.opExtrude","SWEPT_FACE",FACE,{"disambiguationData":[OSD([sQuery(id+"F20.wireOp",EDGE,"E40.left")])]});
            var sketch = newSketch(context, id + "F38", { "sketchPlane" : qUnion([Q0])});
            skLineSegment(sketch, "E66.bottom", {"start": v(-447.68, -685.8) * mm, "end": v(-479.42, -685.8) * mm});
            skLineSegment(sketch, "E66.top", {"start": v(-447.68, -596.9) * mm, "end": v(-479.42, -596.9) * mm});
            skLineSegment(sketch, "E66.left", {"start": v(-444.5, -682.62) * mm, "end": v(-444.5, -600.08) * mm});
            skLineSegment(sketch, "E66.right", {"start": v(-482.6, -682.62) * mm, "end": v(-482.6, -600.08) * mm});
            skPoint(sketch, "E67.visualSharp", {"position": v(-482.6, -596.9) * mm});
            skArc(sketch, "E67.filletArc", {"start": v(-479.42, -596.9) * mm, "mid": v(-481.67, -597.83) * mm, "end": v(-482.6, -600.08) * mm});
            skPoint(sketch, "E68.visualSharp", {"position": v(-482.6, -685.8) * mm});
            skArc(sketch, "E68.filletArc", {"start": v(-482.6, -682.62) * mm, "mid": v(-481.67, -684.87) * mm, "end": v(-479.42, -685.8) * mm});
            skPoint(sketch, "E69.visualSharp", {"position": v(-444.5, -685.8) * mm});
            skArc(sketch, "E69.filletArc", {"start": v(-447.68, -685.8) * mm, "mid": v(-445.43, -684.87) * mm, "end": v(-444.5, -682.62) * mm});
            skPoint(sketch, "E70.visualSharp", {"position": v(-444.5, -596.9) * mm});
            skArc(sketch, "E70.filletArc", {"start": v(-444.5, -600.08) * mm, "mid": v(-445.43, -597.83) * mm, "end": v(-447.68, -596.9) * mm});
            skSolve(sketch);
        }
        {
            var Q0;
            Q0 = qSketchRegion(id + "F38", true);
            extrude(context, id + "F39", {"entities" : qUnion([Q0]), "oppositeDirection" : true, "depth" : 1143 * mm});
        }
        {
            var Q0;
            Q0=makeQuery(id+"F39.opExtrude","SWEPT_BODY",BODY,{"disambiguationData":[OSD([sQuery(id+"F38.wireOp",EDGE,"E66.bottom"),sQuery(id+"F38.wireOp",EDGE,"E66.top"),sQuery(id+"F38.wireOp",EDGE,"E66.left"),sQuery(id+"F38.wireOp",EDGE,"E66.right"),sQuery(id+"F38.wireOp",EDGE,"E67.filletArc"),sQuery(id+"F38.wireOp",EDGE,"E68.filletArc"),sQuery(id+"F38.wireOp",EDGE,"E69.filletArc"),sQuery(id+"F38.wireOp",EDGE,"E70.filletArc")])]});
            deleteBodies(context, id + "F40", {"entities" : qUnion([Q0])});
        }
        {
            var Q0;
            Q0=makeQuery(id+"F35.opExtrude","SWEPT_BODY",BODY,{"disambiguationData":[OSD([sQuery(id+"F34.wireOp",EDGE,"E55.bottom"),sQuery(id+"F34.wireOp",EDGE,"E55.top"),sQuery(id+"F34.wireOp",EDGE,"E55.left"),sQuery(id+"F34.wireOp",EDGE,"E55.right"),sQuery(id+"F34.wireOp",EDGE,"E56.filletArc"),sQuery(id+"F34.wireOp",EDGE,"E57.filletArc"),sQuery(id+"F34.wireOp",EDGE,"E58.filletArc"),sQuery(id+"F34.wireOp",EDGE,"E60.filletArc")])]});
            deleteBodies(context, id + "F41", {"entities" : qUnion([Q0])});
        }
        {
            var Q0;
            Q0=makeQuery(id+"F23.opExtrude","SWEPT_FACE",FACE,{"disambiguationData":[OSD([sQuery(id+"F22.wireOp",EDGE,"E45.right")])]});
            var sketch = newSketch(context, id + "F42", { "sketchPlane" : qUnion([Q0])});
            skLineSegment(sketch, "E71.bottom", {"start": v(41.28, -596.9) * mm, "end": v(123.83, -596.9) * mm});
            skLineSegment(sketch, "E71.top", {"start": v(41.28, -558.8) * mm, "end": v(123.83, -558.8) * mm});
            skLineSegment(sketch, "E71.left", {"start": v(38.1, -593.73) * mm, "end": v(38.1, -561.98) * mm});
            skLineSegment(sketch, "E71.right", {"start": v(127, -593.73) * mm, "end": v(127, -561.98) * mm});
            skPoint(sketch, "E72.visualSharp", {"position": v(38.1, -558.8) * mm});
            skArc(sketch, "E72.filletArc", {"start": v(41.28, -558.8) * mm, "mid": v(39.03, -559.73) * mm, "end": v(38.1, -561.98) * mm});
            skPoint(sketch, "E73.visualSharp", {"position": v(127, -558.8) * mm});
            skArc(sketch, "E73.filletArc", {"start": v(127, -561.98) * mm, "mid": v(126.07, -559.73) * mm, "end": v(123.83, -558.8) * mm});
            skPoint(sketch, "E74.visualSharp", {"position": v(127, -596.9) * mm});
            skArc(sketch, "E74.filletArc", {"start": v(123.83, -596.9) * mm, "mid": v(126.07, -595.97) * mm, "end": v(127, -593.73) * mm});
            skPoint(sketch, "E75.visualSharp", {"position": v(38.1, -596.9) * mm});
            skArc(sketch, "E75.filletArc", {"start": v(38.1, -593.73) * mm, "mid": v(39.03, -595.97) * mm, "end": v(41.28, -596.9) * mm});
            skSolve(sketch);
        }
        {
            var Q0;
            Q0 = qSketchRegion(id + "F42", true);
            extrude(context, id + "F43", {"entities" : qUnion([Q0]), "depth" : 1066.8 * mm});
        }
        {
            var Q0;
            Q0=makeQuery(id+"F43.opExtrude","SWEPT_BODY",BODY,{"disambiguationData":[OSD([sQuery(id+"F42.wireOp",EDGE,"E71.bottom"),sQuery(id+"F42.wireOp",EDGE,"E71.top"),sQuery(id+"F42.wireOp",EDGE,"E71.left"),sQuery(id+"F42.wireOp",EDGE,"E71.right"),sQuery(id+"F42.wireOp",EDGE,"E72.filletArc"),sQuery(id+"F42.wireOp",EDGE,"E73.filletArc"),sQuery(id+"F42.wireOp",EDGE,"E74.filletArc"),sQuery(id+"F42.wireOp",EDGE,"E75.filletArc")])]});
            transform(context, id + "F44", {"entities" : qUnion([Q0]), "transformType" : TransformType.TRANSLATION_3D, "dx" : 0 * mm, "dy" : 88.9 * mm, "dz" : 0 * mm, "makeCopy" : true});
        }
        {
            var Q0;
            Q0=makeQuery(id+"F44.opPattern","COPY",BODY,{"derivedFrom":makeQuery(id+"F43.opExtrude","SWEPT_BODY",BODY,{"disambiguationData":[OSD([sQuery(id+"F42.wireOp",EDGE,"E71.bottom"),sQuery(id+"F42.wireOp",EDGE,"E71.top"),sQuery(id+"F42.wireOp",EDGE,"E71.left"),sQuery(id+"F42.wireOp",EDGE,"E71.right"),sQuery(id+"F42.wireOp",EDGE,"E72.filletArc"),sQuery(id+"F42.wireOp",EDGE,"E73.filletArc"),sQuery(id+"F42.wireOp",EDGE,"E74.filletArc"),sQuery(id+"F42.wireOp",EDGE,"E75.filletArc")])]}),"instanceName":"1"});
            transform(context, id + "F45", {"entities" : qUnion([Q0]), "transformType" : TransformType.TRANSLATION_3D, "dx" : 0 * mm, "dy" : 88.9 * mm, "dz" : 0 * mm, "makeCopy" : true});
        }
        {
            var Q0;
            Q0=makeQuery(id+"F45.opPattern","COPY",BODY,{"derivedFrom":makeQuery(id+"F44.opPattern","COPY",BODY,{"derivedFrom":makeQuery(id+"F43.opExtrude","SWEPT_BODY",BODY,{"disambiguationData":[OSD([sQuery(id+"F42.wireOp",EDGE,"E71.bottom"),sQuery(id+"F42.wireOp",EDGE,"E71.top"),sQuery(id+"F42.wireOp",EDGE,"E71.left"),sQuery(id+"F42.wireOp",EDGE,"E71.right"),sQuery(id+"F42.wireOp",EDGE,"E72.filletArc"),sQuery(id+"F42.wireOp",EDGE,"E73.filletArc"),sQuery(id+"F42.wireOp",EDGE,"E74.filletArc"),sQuery(id+"F42.wireOp",EDGE,"E75.filletArc")])]}),"instanceName":"1"}),"instanceName":"1"});
            transform(context, id + "F46", {"entities" : qUnion([Q0]), "transformType" : TransformType.TRANSLATION_3D, "dx" : 0 * mm, "dy" : 88.9 * mm, "dz" : 0 * mm, "makeCopy" : true});
        }
        {
            var Q0;
            Q0=makeQuery(id+"F21.opExtrude","SWEPT_FACE",FACE,{"disambiguationData":[OSD([sQuery(id+"F20.wireOp",EDGE,"E40.right")])]});
            var sketch = newSketch(context, id + "F47", { "sketchPlane" : qUnion([Q0])});
            skLineSegment(sketch, "E76.bottom", {"start": v(396.88, -596.9) * mm, "end": v(441.33, -596.9) * mm});
            skLineSegment(sketch, "E76.top", {"start": v(396.88, -558.8) * mm, "end": v(441.32, -558.8) * mm});
            skLineSegment(sketch, "E76.left", {"start": v(393.7, -593.73) * mm, "end": v(393.7, -561.98) * mm});
            skLineSegment(sketch, "E76.right", {"start": v(444.5, -593.73) * mm, "end": v(444.5, -561.98) * mm});
            skPoint(sketch, "E77.visualSharp", {"position": v(393.7, -596.9) * mm});
            skArc(sketch, "E77.filletArc", {"start": v(393.7, -593.73) * mm, "mid": v(394.63, -595.97) * mm, "end": v(396.88, -596.9) * mm});
            skPoint(sketch, "E78.visualSharp", {"position": v(444.5, -596.9) * mm});
            skArc(sketch, "E78.filletArc", {"start": v(441.33, -596.9) * mm, "mid": v(443.57, -595.97) * mm, "end": v(444.5, -593.73) * mm});
            skPoint(sketch, "E79.visualSharp", {"position": v(444.5, -558.8) * mm});
            skArc(sketch, "E79.filletArc", {"start": v(444.5, -561.98) * mm, "mid": v(443.57, -559.73) * mm, "end": v(441.32, -558.8) * mm});
            skPoint(sketch, "E80.visualSharp", {"position": v(393.7, -558.8) * mm});
            skArc(sketch, "E80.filletArc", {"start": v(396.88, -558.8) * mm, "mid": v(394.63, -559.73) * mm, "end": v(393.7, -561.98) * mm});
            skSolve(sketch);
        }
        {
            var Q0;
            Q0 = qSketchRegion(id + "F47", true);
            extrude(context, id + "F48", {"entities" : qUnion([Q0]), "depth" : 1066.8 * mm});
        }
    });
